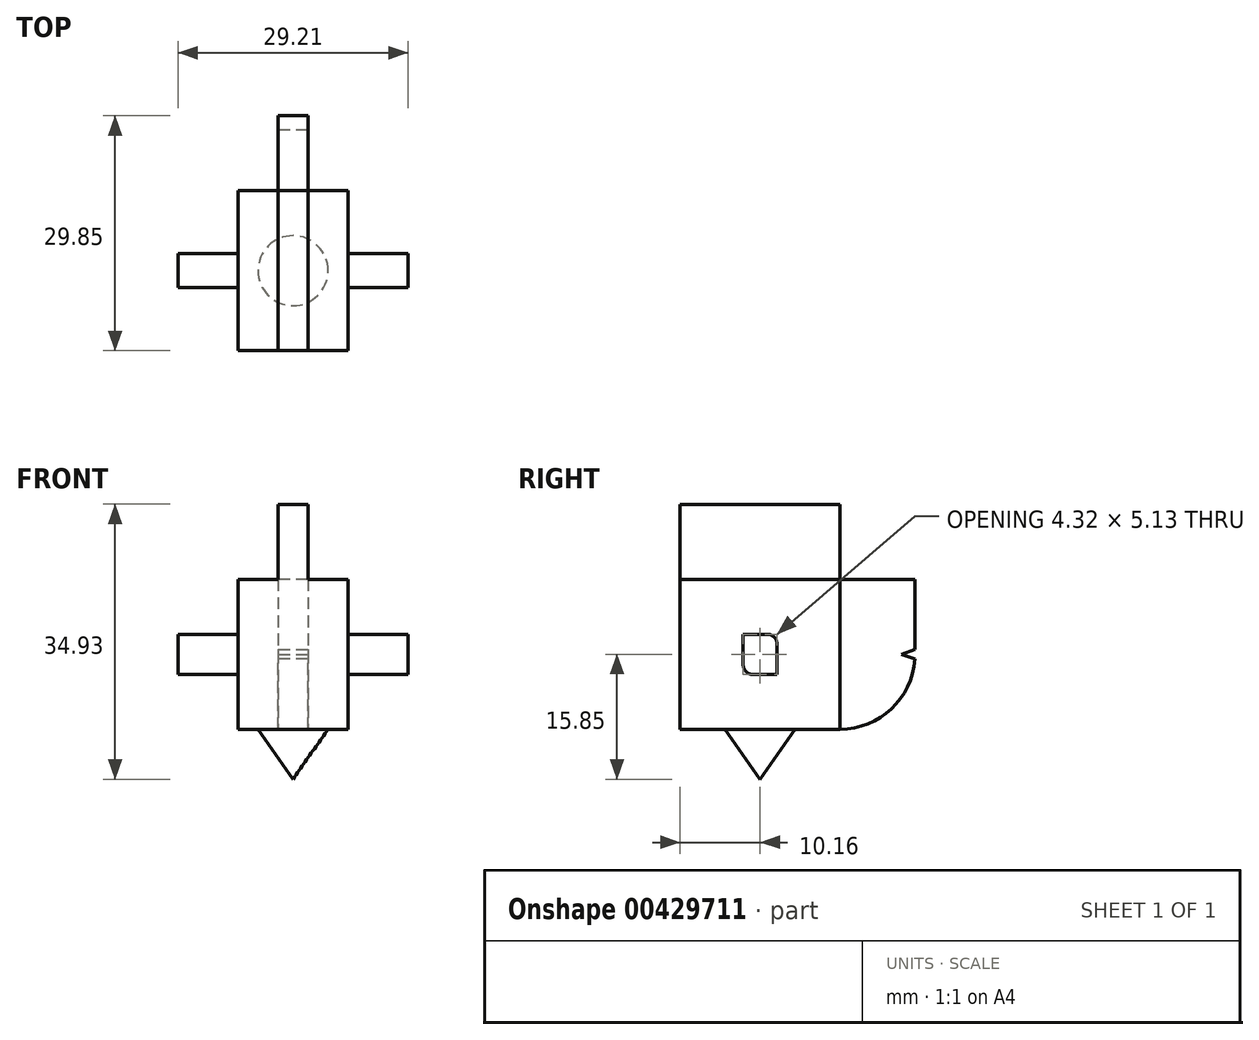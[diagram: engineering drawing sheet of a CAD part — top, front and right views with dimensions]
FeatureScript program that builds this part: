
annotation { "Feature Type Name" : "Feature", "Feature Type Description" : "" }
export const myFeature = defineFeature(function(context is Context, id is Id, definition is map)
    precondition{}
    {
        {
            var Q0;
            Q0=qCreatedBy(makeId("Right.planeOp"),FACE);
            var sketch = newSketch(context, id + "F0", { "sketchPlane" : qUnion([Q0])});
            skLineSegment(sketch, "E0.bottom", {"start": v(0, 0) * mm, "end": v(20.32, 0) * mm});
            skLineSegment(sketch, "E0.top", {"start": v(0, -19.05) * mm, "end": v(20.32, -19.05) * mm});
            skLineSegment(sketch, "E0.left", {"start": v(0, 0) * mm, "end": v(0, -19.05) * mm});
            skLineSegment(sketch, "E0.right", {"start": v(20.32, 0) * mm, "end": v(20.32, -19.05) * mm});
            skSolve(sketch);
        }
        {
            var Q0;
            Q0=makeQuery(id+"F0.imprint","IMPRINT",FACE,{"disambiguationData":[TD([[makeQuery(id+"F0.imprint","IMPRINT",EDGE,{"derivedFrom":sQuery(id+"F0.wireOp",EDGE,"E0.bottom")}),-1.0]])]});
            extrude(context, id + "F1", {"entities" : qUnion([Q0]), "depth" : 13.97 * mm});
        }
        {
            var Q0;
            Q0=makeQuery(id+"F1.opExtrude","SWEPT_FACE",FACE,{"disambiguationData":[OSD([sQuery(id+"F0.wireOp",EDGE,"E0.bottom")])]});
            var sketch = newSketch(context, id + "F2", { "sketchPlane" : qUnion([Q0])});
            skLineSegment(sketch, "E1.bottom", {"start": v(-7.62, 12.32) * mm, "end": v(21.6, 12.32) * mm});
            skLineSegment(sketch, "E1.top", {"start": v(-7.62, 8) * mm, "end": v(21.6, 8) * mm});
            skLineSegment(sketch, "E1.left", {"start": v(-7.62, 12.32) * mm, "end": v(-7.62, 8) * mm});
            skLineSegment(sketch, "E1.right", {"start": v(21.6, 12.32) * mm, "end": v(21.6, 8) * mm});
            skSolve(sketch);
        }
        {
            var Q0;
            Q0 = qSketchRegion(id + "F2", true);
            extrude(context, id + "F3", {"entities" : qUnion([Q0]), "operationType" : NewBodyOperationType.ADD, "oppositeDirection" : true, "depth" : 12.12 * mm, "hasSecondDirection" : true, "secondDirectionOppositeDirection" : true, "secondDirectionDepth" : 7 * mm});
        }
        {
            var Q0;
            Q0=qCreatedBy(makeId("Right.planeOp"),FACE);
            cPlane(context, id + "F4", {"entities" : qUnion([Q0]), "cplaneType" : CPlaneType.OFFSET, "offset" : 7 * mm, "width" : 152.4 * mm, "height" : 152.4 * mm});
        }
        {
            var Q0;
            Q0=qCreatedBy(id+"F4.planeOp",FACE);
            var sketch = newSketch(context, id + "F5", { "sketchPlane" : qUnion([Q0])});
            skLineSegment(sketch, "E2", {"start": v(5.71, -19.05) * mm, "end": v(10.16, -25.4) * mm});
            skLineSegment(sketch, "E3", {"start": v(10.16, -25.4) * mm, "end": v(14.6, -19.05) * mm});
            skLineSegment(sketch, "E4", {"start": v(14.6, -19.05) * mm, "end": v(5.71, -19.05) * mm});
            skLineSegment(sketch, "E5", {"start": v(10.16, -25.4) * mm, "end": v(10.16, -19.05) * mm});
            skSolve(sketch);
        }
        {
            var Q0;
            {var subQ0=sQuery(id+"F5.wireOp",EDGE,"E2");Q0=makeQuery(id+"F5.imprint","IMPRINT",FACE,{"disambiguationData":[TD([[makeQuery(id+"F5.imprint","IMPRINT",EDGE,{"derivedFrom":subQ0}),1.0]])]});}
            var Q1;
            Q1=sQuery(id+"F5.wireOp",EDGE,"E5");
            revolve(context, id + "F6", {"operationType" : NewBodyOperationType.ADD, "entities" : qUnion([Q0]), "axis" : qUnion([Q1]), "revolveType" : RevolveType.FULL});
        }
        {
            var Q0;
            Q0=qCreatedBy(id+"F4.planeOp",FACE);
            var sketch = newSketch(context, id + "F7", { "sketchPlane" : qUnion([Q0])});
            skCircle(sketch, "E6", {"center": v(20.32, -9.53) * mm, "radius": 9.53 * mm});
            skLineSegment(sketch, "E7", {"start": v(20.32, -9.53) * mm, "end": v(29.85, -9.53) * mm});
            skLineSegment(sketch, "E8", {"start": v(20.32, -9.53) * mm, "end": v(20.32, -19.05) * mm});
            skLineSegment(sketch, "E9.bottom", {"start": v(20.32, 0) * mm, "end": v(0, 0) * mm});
            skLineSegment(sketch, "E9.top", {"start": v(20.32, 9.53) * mm, "end": v(0, 9.53) * mm});
            skLineSegment(sketch, "E9.left", {"start": v(20.32, 0) * mm, "end": v(20.32, 9.53) * mm});
            skLineSegment(sketch, "E9.right", {"start": v(0, 0) * mm, "end": v(0, 9.52) * mm});
            skSolve(sketch);
        }
        {
            var Q0;
            {var subQ0=sQuery(id+"F7.wireOp",EDGE,"E7");Q0=makeQuery(id+"F7.imprint","IMPRINT",FACE,{"disambiguationData":[TD([[makeQuery(id+"F7.imprint","IMPRINT",EDGE,{"derivedFrom":subQ0}),-1.0]])]});}
            var Q1;
            Q1=makeQuery(id+"F7.imprint","IMPRINT",FACE,{"disambiguationData":[TD([[makeQuery(id+"F7.imprint","IMPRINT",EDGE,{"derivedFrom":sQuery(id+"F7.wireOp",EDGE,"E9.bottom")}),-1.0]])]});
            extrude(context, id + "F8", {"entities" : qUnion([Q0, Q1]), "operationType" : NewBodyOperationType.ADD, "endBound" : BoundingType.SYMMETRIC, "depth" : 3.8 * mm});
        }
        {
            var Q0;
            Q0=makeQuery(id+"F8.opExtrude","SWEPT_FACE",FACE,{"disambiguationData":[OSD([sQuery(id+"F7.wireOp",EDGE,"E7")])]});
            var Q1;
            Q1=makeQuery(id+"F1.opExtrude","SWEPT_FACE",FACE,{"disambiguationData":[OSD([sQuery(id+"F0.wireOp",EDGE,"E0.bottom")])]});
            extrude(context, id + "F9", {"entities" : qUnion([Q0]), "operationType" : NewBodyOperationType.ADD, "endBound" : BoundingType.UP_TO_SURFACE, "endBoundEntityFace" : qUnion([Q1]), "depth" : 25.4 * mm});
        }
        {
            var Q0;
            {var subQ0=sQuery(id+"F2.wireOp",EDGE,"E1.right");var subQ1=sQuery(id+"F2.wireOp",EDGE,"E1.top");Q0=makeQuery(id+"F3.boolean.opBoolean","SPLIT",EDGE,{"disambiguationData":[TD([makeQuery(id+"F3.opExtrude","SWEPT_FACE",FACE,{"disambiguationData":[OSD([subQ0])]})])],"derivedFrom":makeQuery(id+"F3.opExtrude","CAP_EDGE",EDGE,{"disambiguationData":[OSD([subQ1])],"isStart":false})});}
            var Q1;
            {var subQ0=sQuery(id+"F2.wireOp",EDGE,"E1.bottom");var subQ1=sQuery(id+"F2.wireOp",EDGE,"E1.right");Q1=makeQuery(id+"F3.boolean.opBoolean","SPLIT",EDGE,{"disambiguationData":[TD([makeQuery(id+"F3.opExtrude","SWEPT_FACE",FACE,{"disambiguationData":[OSD([subQ1])]})])],"derivedFrom":makeQuery(id+"F3.opExtrude","CAP_EDGE",EDGE,{"disambiguationData":[OSD([subQ0])],"isStart":true})});}
            var Q2;
            {var subQ0=sQuery(id+"F2.wireOp",EDGE,"E1.top");var subQ1=sQuery(id+"F2.wireOp",EDGE,"E1.left");Q2=makeQuery(id+"F3.boolean.opBoolean","SPLIT",EDGE,{"disambiguationData":[TD([makeQuery(id+"F3.opExtrude","SWEPT_FACE",FACE,{"disambiguationData":[OSD([subQ1])]})])],"derivedFrom":makeQuery(id+"F3.opExtrude","CAP_EDGE",EDGE,{"disambiguationData":[OSD([subQ0])],"isStart":false})});}
            var Q3;
            {var subQ0=sQuery(id+"F2.wireOp",EDGE,"E1.bottom");var subQ1=sQuery(id+"F2.wireOp",EDGE,"E1.left");Q3=makeQuery(id+"F3.boolean.opBoolean","SPLIT",EDGE,{"disambiguationData":[TD([makeQuery(id+"F3.opExtrude","SWEPT_FACE",FACE,{"disambiguationData":[OSD([subQ1])]})])],"derivedFrom":makeQuery(id+"F3.opExtrude","CAP_EDGE",EDGE,{"disambiguationData":[OSD([subQ0])],"isStart":true})});}
            var Q4;
            Q4=makeQuery(id+"F9.opExtrude","TWEAK_EDGE",EDGE,{"derivedFrom":[makeQuery(id+"F1.opExtrude","SWEPT_FACE",FACE,{"disambiguationData":[OSD([sQuery(id+"F0.wireOp",EDGE,"E0.bottom")])]}),makeQuery(id+"F8.opExtrude","SWEPT_EDGE",EDGE,{"disambiguationData":[OSD([sQuery(id+"F7.wireOp",EDGE,"E6"),sQuery(id+"F7.wireOp",EDGE,"E7")])]})]});
            fillet(context, id + "F10", {"entities" : qUnion([Q0, Q1, Q2, Q3, Q4]), "radius" : 1.27 * mm, "tangentPropagation" : true, "allowEdgeOverflow" : false});
        }
        {
            var Q0;
            Q0=qCreatedBy(id+"F4.planeOp",FACE);
            var sketch = newSketch(context, id + "F11", { "sketchPlane" : qUnion([Q0])});
            skLineSegment(sketch, "E10", {"start": v(29.84, -8.9) * mm, "end": v(28.1, -9.53) * mm});
            skLineSegment(sketch, "E11", {"start": v(28.1, -9.52) * mm, "end": v(29.84, -10.16) * mm});
            skLineSegment(sketch, "E12", {"start": v(29.85, -10.16) * mm, "end": v(29.85, -8.9) * mm});
            skSolve(sketch);
        }
        {
            var Q0;
            Q0 = qSketchRegion(id + "F11", true);
            extrude(context, id + "F12", {"entities" : qUnion([Q0]), "operationType" : NewBodyOperationType.REMOVE, "endBound" : BoundingType.SYMMETRIC, "oppositeDirection" : true, "depth" : 50.8 * mm});
        }
    });
